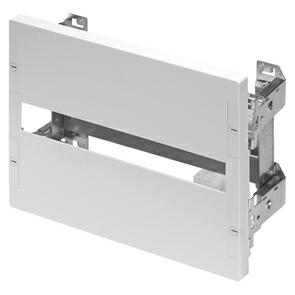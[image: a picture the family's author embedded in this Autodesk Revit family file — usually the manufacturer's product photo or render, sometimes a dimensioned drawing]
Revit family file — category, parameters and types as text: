
# Revit family: Building-ContenitoriParete-GEWISS-46-PANNELLI_PER_MSS_MTX
name_source: partatom
category: Attrezzatura elettrica
revit_build: Autodesk Revit 2016 (Build: 20161004_0715(x64)
units: mm (PartAtom-declared; Revit-internal decimal feet)

## family parameters
Basato su piano di lavoro = Sì
Condiviso = No
Configurazione quadro = Due colonne, circuiti in orizzontale
Numero OmniClass = 23.80.30.11.17
Punto di calcolo locali = Sì
Quota connettore circolare = Usa diametro
Sempre verticale = No
Taglio con vuoti quando caricato = No
Tipo di parte = Pannello comandi
Titolo OmniClass = Distribution Boards and Control Panels

## types (1)
- Building-ContenitoriParete-GEWISS-46-PANNELLI_PER_MSS_MTX
    Adatto per: = 46QP - 46QM - 46QX
    Altezza = 2 Moduli
    Catalogo = BUILDING
    Catalogo Serie = 46 QP
    Codice EAN = 8011564284388
    Codice Electrocod = 0303
    Colore = Grigio RAL 7035
    Descrizione = KIT PER MTX160c-160-250+BD/MSS160 7GR
    Dotazioni = Accessori di fissaggio
    Fissaggio apparecchiature = piastra con guida DIN EN 50022
    GEWISS SCHEDA TECNICA = http://pro.gewiss.com
    H_pannello = 300 mm
    IDF = bb269f62-5bcb-4c80-a0b0-a9478541477d
    IDT = acce35f6-ac00-4ae3-99d6-2321acd460a7
    Immagine tipo = GW10016174.jpg
    Lunghezza pannello = 718 mm  [stored 2.35564 ft]
    Modello = GW46573F
    Pannello = GEWISS - GRIGIO RAL 7035
    Per quadri base (mm) = 800
    Posizione del differenziale = a "L"
    Produttore = GEWISS S.p.A.
    Prospetto di default = 1219 mm
    SEO = Kit scatolati
    Scheda Tecnica = https://www.gewiss.com
    Spessore pannello = 15 mm  [stored 0.0492126 ft]
    Tipo scatolato MTX = MTX 160c - MTX 160 - MTX 250
    Tipo sezionatore MSS = MSS 160
    URL = https://www.gewiss.com
    Versione file RFA = 18.0

note: [stored X ft] marks values corroborated as IEEE doubles in the binary element streams (Revit-internal decimal feet)
